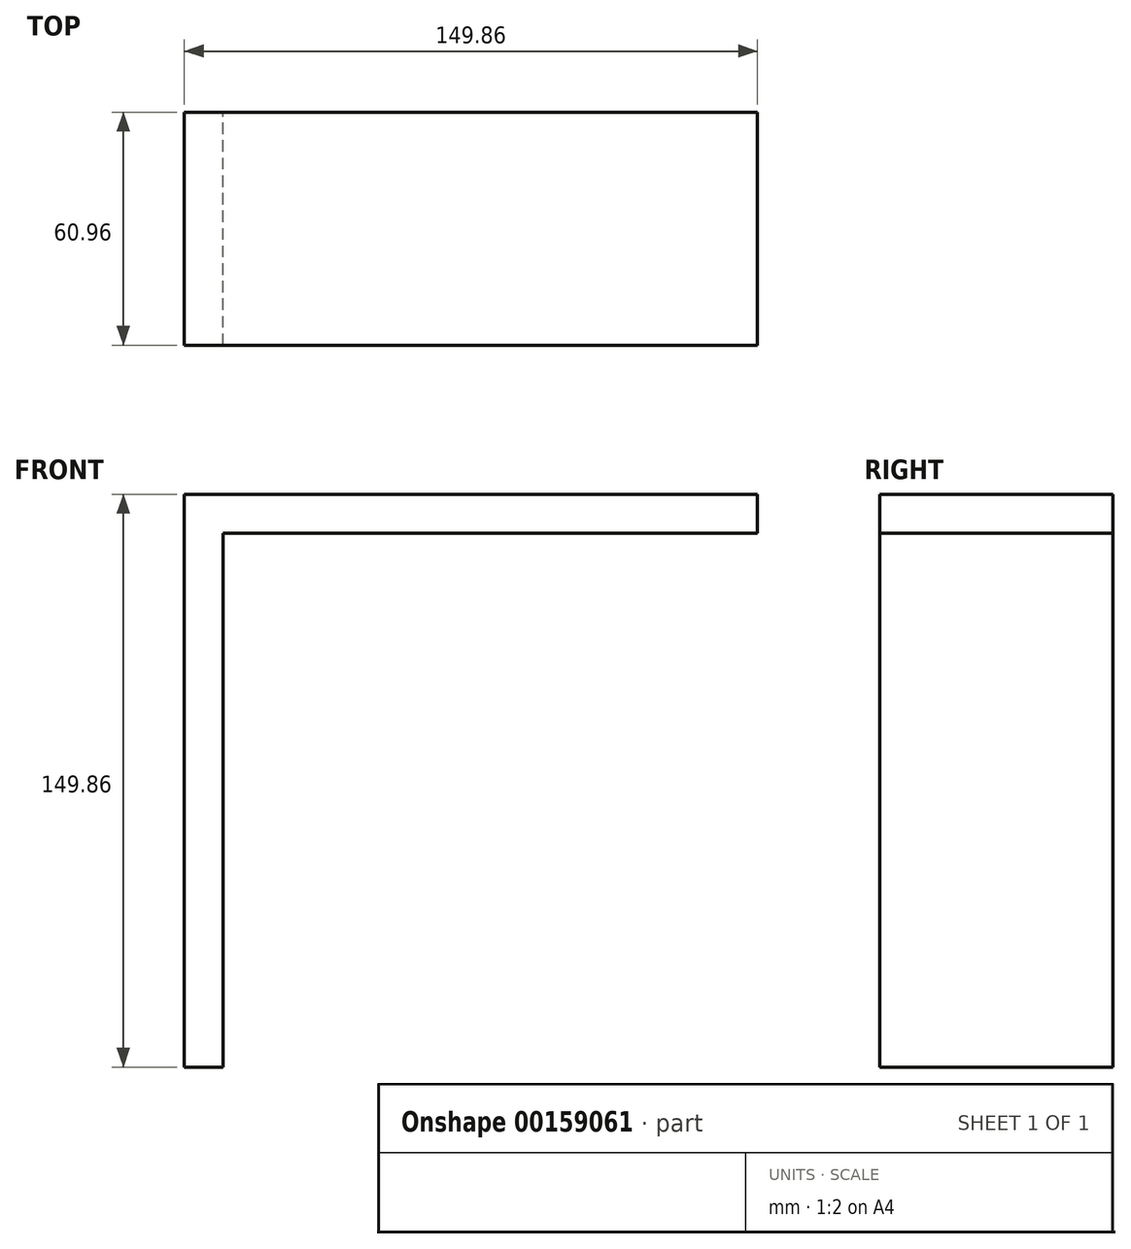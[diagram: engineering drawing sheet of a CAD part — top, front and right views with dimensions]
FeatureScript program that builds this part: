
annotation { "Feature Type Name" : "Feature", "Feature Type Description" : "" }
export const myFeature = defineFeature(function(context is Context, id is Id, definition is map)
    precondition{}
    {
        {
            var Q0;
            Q0=qCreatedBy(makeId("Front.planeOp"),FACE);
            var sketch = newSketch(context, id + "F0", { "sketchPlane" : qUnion([Q0])});
            skLineSegment(sketch, "E0", {"start": v(0, 83.56) * mm, "end": v(0, -80.57) * mm, "construction": true});
            skLineSegment(sketch, "E1", {"start": v(92.77, 0) * mm, "end": v(-170.9, 0) * mm, "construction": true});
            skLineSegment(sketch, "E2", {"start": v(0, 70.2) * mm, "end": v(-149.86, 70.2) * mm});
            skLineSegment(sketch, "E3", {"start": v(-149.86, 70.2) * mm, "end": v(-149.86, -79.67) * mm});
            skLineSegment(sketch, "E4", {"start": v(-149.86, -79.67) * mm, "end": v(-139.7, -79.67) * mm});
            skLineSegment(sketch, "E5", {"start": v(-139.7, -79.67) * mm, "end": v(-139.7, 60.03) * mm});
            skLineSegment(sketch, "E6", {"start": v(-139.7, 60.03) * mm, "end": v(0, 60.03) * mm});
            skLineSegment(sketch, "E7", {"start": v(0, 70.2) * mm, "end": v(0, 60.03) * mm});
            skSolve(sketch);
        }
        {
            var Q0;
            Q0 = qSketchRegion(id + "F0", true);
            extrude(context, id + "F1", {"entities" : qUnion([Q0]), "depth" : 60.96 * mm});
        }
    });
